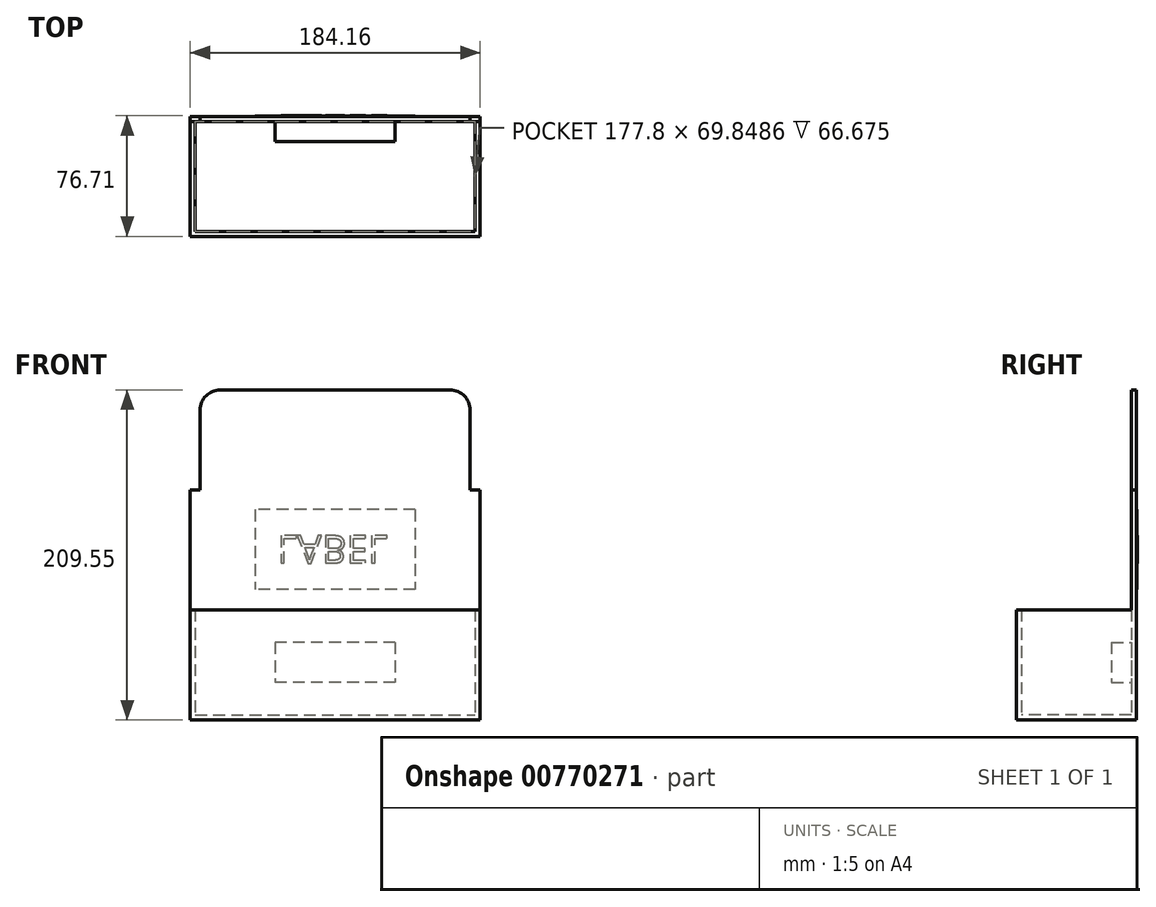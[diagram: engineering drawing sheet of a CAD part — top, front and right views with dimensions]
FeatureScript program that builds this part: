
annotation { "Feature Type Name" : "Feature", "Feature Type Description" : "" }
export const myFeature = defineFeature(function(context is Context, id is Id, definition is map)
    precondition{}
    {
        {
            var Q0;
            Q0=qCreatedBy(makeId("Top.planeOp"),FACE);
            var sketch = newSketch(context, id + "F0", { "sketchPlane" : qUnion([Q0])});
            skLineSegment(sketch, "E0.bottom", {"start": v(92.08, 38.1) * mm, "end": v(-92.08, 38.1) * mm});
            skLineSegment(sketch, "E0.top", {"start": v(92.08, -38.1) * mm, "end": v(-92.08, -38.1) * mm});
            skLineSegment(sketch, "E0.left", {"start": v(92.08, 38.1) * mm, "end": v(92.08, -38.1) * mm});
            skLineSegment(sketch, "E0.right", {"start": v(-92.08, 38.1) * mm, "end": v(-92.08, -38.1) * mm});
            skPoint(sketch, "E0.middle", {"position": v(0, 0) * mm});
            skSolve(sketch);
        }
        {
            var Q0;
            Q0=qSketchRegion(id+"F0",true);
            extrude(context, id + "F1", {"entities" : qUnion([Q0]), "depth" : 3.17 * mm});
        }
        {
            var Q0;
            Q0=makeQuery(id+"F1.opExtrude","CAP_FACE",FACE,{"disambiguationData":[OSD([sQuery(id+"F0.wireOp",EDGE,"E0.bottom"),sQuery(id+"F0.wireOp",EDGE,"E0.top"),sQuery(id+"F0.wireOp",EDGE,"E0.left"),sQuery(id+"F0.wireOp",EDGE,"E0.right")])],"isStart":false});
            var sketch = newSketch(context, id + "F2", { "sketchPlane" : qUnion([Q0])});
            skLineSegment(sketch, "E1.bottom", {"start": v(-92.08, 38.1) * mm, "end": v(-88.9, 38.1) * mm});
            skLineSegment(sketch, "E1.top", {"start": v(-92.08, -38.1) * mm, "end": v(-88.9, -38.1) * mm});
            skLineSegment(sketch, "E1.left", {"start": v(-92.08, 38.1) * mm, "end": v(-92.08, -38.1) * mm});
            skLineSegment(sketch, "E1.right", {"start": v(-88.9, 38.1) * mm, "end": v(-88.9, -38.1) * mm});
            skLineSegment(sketch, "E2.MirrorCS", {"start": v(92.08, 38.1) * mm, "end": v(88.9, 38.1) * mm});
            skLineSegment(sketch, "E3.MirrorCS", {"start": v(88.9, 38.1) * mm, "end": v(88.9, -38.1) * mm});
            skLineSegment(sketch, "E4.MirrorCS", {"start": v(92.08, 38.1) * mm, "end": v(92.08, -38.1) * mm});
            skLineSegment(sketch, "E5.MirrorCS", {"start": v(92.08, -38.1) * mm, "end": v(88.9, -38.1) * mm});
            skLineSegment(sketch, "E6.bottom", {"start": v(-88.9, 38.1) * mm, "end": v(88.9, 38.1) * mm});
            skLineSegment(sketch, "E6.top", {"start": v(-88.9, 34.92) * mm, "end": v(88.9, 34.92) * mm});
            skLineSegment(sketch, "E6.left", {"start": v(-88.9, 38.1) * mm, "end": v(-88.9, 34.92) * mm});
            skLineSegment(sketch, "E6.right", {"start": v(88.9, 38.1) * mm, "end": v(88.9, 34.92) * mm});
            skLineSegment(sketch, "E7.MirrorCS", {"start": v(-88.9, -34.92) * mm, "end": v(88.9, -34.92) * mm});
            skLineSegment(sketch, "E8.MirrorCS", {"start": v(-88.9, -38.1) * mm, "end": v(88.9, -38.1) * mm});
            skSolve(sketch);
        }
        {
            var Q0;
            Q0=qSketchRegion(id+"F2",true);
            extrude(context, id + "F3", {"entities" : qUnion([Q0]), "operationType" : NewBodyOperationType.ADD, "depth" : 66.67 * mm});
        }
        {
            var Q0;
            Q0=makeQuery(id+"F3.opExtrude","CAP_FACE",FACE,{"disambiguationData":[OSD([sQuery(id+"F2.wireOp",EDGE,"E1.bottom"),sQuery(id+"F2.wireOp",EDGE,"E1.top"),sQuery(id+"F2.wireOp",EDGE,"E1.left"),sQuery(id+"F2.wireOp",EDGE,"E1.right"),sQuery(id+"F2.wireOp",EDGE,"E2.MirrorCS"),sQuery(id+"F2.wireOp",EDGE,"E3.MirrorCS"),sQuery(id+"F2.wireOp",EDGE,"E4.MirrorCS"),sQuery(id+"F2.wireOp",EDGE,"E5.MirrorCS"),sQuery(id+"F2.wireOp",EDGE,"E6.bottom"),sQuery(id+"F2.wireOp",EDGE,"E6.top"),sQuery(id+"F2.wireOp",EDGE,"E7.MirrorCS"),sQuery(id+"F2.wireOp",EDGE,"E8.MirrorCS")])],"isStart":false});
            var sketch = newSketch(context, id + "F4", { "sketchPlane" : qUnion([Q0])});
            skLineSegment(sketch, "E9.bottom", {"start": v(-92.08, 38.1) * mm, "end": v(92.08, 38.1) * mm});
            skLineSegment(sketch, "E9.top", {"start": v(-92.08, 34.92) * mm, "end": v(92.08, 34.92) * mm});
            skLineSegment(sketch, "E9.left", {"start": v(-92.08, 38.1) * mm, "end": v(-92.08, 34.92) * mm});
            skLineSegment(sketch, "E9.right", {"start": v(92.08, 38.1) * mm, "end": v(92.08, 34.92) * mm});
            skSolve(sketch);
        }
        {
            var Q0;
            Q0=qSketchRegion(id+"F4",true);
            extrude(context, id + "F5", {"entities" : qUnion([Q0]), "operationType" : NewBodyOperationType.ADD, "depth" : 76.2 * mm});
        }
        {
            var Q0;
            Q0=makeQuery(id+"F5.opExtrude","CAP_FACE",FACE,{"disambiguationData":[OSD([sQuery(id+"F4.wireOp",EDGE,"E9.bottom"),sQuery(id+"F4.wireOp",EDGE,"E9.top"),sQuery(id+"F4.wireOp",EDGE,"E9.left"),sQuery(id+"F4.wireOp",EDGE,"E9.right")])],"isStart":false});
            var sketch = newSketch(context, id + "F6", { "sketchPlane" : qUnion([Q0])});
            skLineSegment(sketch, "E10.bottom", {"start": v(-85.72, 38.1) * mm, "end": v(85.72, 38.1) * mm});
            skLineSegment(sketch, "E10.top", {"start": v(-85.72, 34.92) * mm, "end": v(85.72, 34.92) * mm});
            skLineSegment(sketch, "E10.left", {"start": v(-85.72, 38.1) * mm, "end": v(-85.72, 34.92) * mm});
            skLineSegment(sketch, "E10.right", {"start": v(85.72, 38.1) * mm, "end": v(85.72, 34.92) * mm});
            skSolve(sketch);
        }
        {
            var Q0;
            Q0=qSketchRegion(id+"F6",true);
            extrude(context, id + "F7", {"entities" : qUnion([Q0]), "operationType" : NewBodyOperationType.ADD, "depth" : 63.5 * mm});
        }
        {
            var Q0;
            Q0=makeQuery(id+"F7.opExtrude","CAP_EDGE",EDGE,{"disambiguationData":[OSD([sQuery(id+"F6.wireOp",EDGE,"E10.left")])],"isStart":false});
            var Q1;
            Q1=makeQuery(id+"F7.opExtrude","CAP_EDGE",EDGE,{"disambiguationData":[OSD([sQuery(id+"F6.wireOp",EDGE,"E10.right")])],"isStart":false});
            fillet(context, id + "F8", {"entities" : qUnion([Q0, Q1]), "radius" : 12.7 * mm, "tangentPropagation" : true, "allowEdgeOverflow" : false});
        }
        {
            var Q0;
            Q0=makeQuery(id+"F7.boolean.opBoolean","MERGE",FACE,{"derivedFrom":[makeQuery(id+"F5.boolean.opBoolean","MERGE",FACE,{"derivedFrom":[makeQuery(id+"F3.opExtrude","SWEPT_FACE",FACE,{"disambiguationData":[OSD([sQuery(id+"F2.wireOp",EDGE,"E6.top")])]}),makeQuery(id+"F5.opExtrude","SWEPT_FACE",FACE,{"disambiguationData":[OSD([sQuery(id+"F4.wireOp",EDGE,"E9.top")])]})]}),makeQuery(id+"F7.opExtrude","SWEPT_FACE",FACE,{"disambiguationData":[OSD([sQuery(id+"F6.wireOp",EDGE,"E10.top")])]})]});
            var sketch = newSketch(context, id + "F9", { "sketchPlane" : qUnion([Q0])});
            skLineSegment(sketch, "E11.bottom", {"start": v(38.1, 49.21) * mm, "end": v(-38.1, 49.21) * mm});
            skLineSegment(sketch, "E11.top", {"start": v(38.1, 23.81) * mm, "end": v(-38.1, 23.81) * mm});
            skLineSegment(sketch, "E11.left", {"start": v(38.1, 49.21) * mm, "end": v(38.1, 23.81) * mm});
            skLineSegment(sketch, "E11.right", {"start": v(-38.1, 49.21) * mm, "end": v(-38.1, 23.81) * mm});
            skPoint(sketch, "E11.middle", {"position": v(0, 36.51) * mm});
            skSolve(sketch);
        }
        {
            var Q0;
            Q0=makeQuery(id+"F9.imprint","IMPRINT",FACE,{"disambiguationData":[TD([[makeQuery(id+"F9.imprint","IMPRINT",EDGE,{"derivedFrom":sQuery(id+"F9.wireOp",EDGE,"E11.bottom")}),1.0]])]});
            extrude(context, id + "F10", {"entities" : qUnion([Q0]), "operationType" : NewBodyOperationType.ADD, "depth" : 12.7 * mm});
        }
        {
            var Q0;
            Q0=makeQuery(id+"F7.boolean.opBoolean","MERGE",FACE,{"derivedFrom":[makeQuery(id+"F5.boolean.opBoolean","MERGE",FACE,{"derivedFrom":[makeQuery(id+"F3.boolean.opBoolean","MERGE",FACE,{"derivedFrom":[makeQuery(id+"F1.opExtrude","SWEPT_FACE",FACE,{"disambiguationData":[OSD([sQuery(id+"F0.wireOp",EDGE,"E0.bottom")])]}),makeQuery(id+"F3.opExtrude","SWEPT_FACE",FACE,{"disambiguationData":[OSD([sQuery(id+"F2.wireOp",EDGE,"E1.bottom"),sQuery(id+"F2.wireOp",EDGE,"E2.MirrorCS"),sQuery(id+"F2.wireOp",EDGE,"E6.bottom")])]})]}),makeQuery(id+"F5.opExtrude","SWEPT_FACE",FACE,{"disambiguationData":[OSD([sQuery(id+"F4.wireOp",EDGE,"E9.bottom")])]})]}),makeQuery(id+"F7.opExtrude","SWEPT_FACE",FACE,{"disambiguationData":[OSD([sQuery(id+"F6.wireOp",EDGE,"E10.bottom")])]})]});
            var sketch = newSketch(context, id + "F11", { "sketchPlane" : qUnion([Q0])});
            skLineSegment(sketch, "E12", {"start": v(-85.72, 146.05) * mm, "end": v(85.72, 146.05) * mm});
            skLineSegment(sketch, "E13", {"start": v(92.07, 70.1) * mm, "end": v(-92.07, 70.1) * mm});
            skLineSegment(sketch, "E14", {"start": v(0, 70.1) * mm, "end": v(0, 146.05) * mm});
            skLineSegment(sketch, "E15.bottom", {"start": v(-50.8, 133.47) * mm, "end": v(50.8, 133.47) * mm});
            skLineSegment(sketch, "E15.top", {"start": v(-50.8, 82.67) * mm, "end": v(50.8, 82.67) * mm});
            skLineSegment(sketch, "E15.left", {"start": v(-50.8, 133.47) * mm, "end": v(-50.8, 82.67) * mm});
            skLineSegment(sketch, "E15.right", {"start": v(50.8, 133.47) * mm, "end": v(50.8, 82.67) * mm});
            skPoint(sketch, "E15.middle", {"position": v(0, 108.07) * mm});
            skSolve(sketch);
        }
        {
            var Q0;
            Q0=qSketchRegion(id+"F11",true);
            extrude(context, id + "F12", {"entities" : qUnion([Q0]), "operationType" : NewBodyOperationType.ADD, "depth" : 0.25 * mm});
        }
        {
            var Q0;
            Q0=makeQuery(id+"F12.opExtrude","CAP_FACE",FACE,{"disambiguationData":[OSD([sQuery(id+"F11.wireOp",EDGE,"E15.bottom"),sQuery(id+"F11.wireOp",EDGE,"E15.top"),sQuery(id+"F11.wireOp",EDGE,"E15.left"),sQuery(id+"F11.wireOp",EDGE,"E15.right")])],"isStart":false});
            var sketch = newSketch(context, id + "F13", { "sketchPlane" : qUnion([Q0])});
            skText(sketch, "E16", { "text": "LABEL", "fontName": "OpenSans-Regular.ttf"});
            const initialGuessF13  = {"E16": [0.03675, 0.11698, -1, 0, 0.01757]};
            skSetInitialGuess(sketch, initialGuessF13);
            skSolve(sketch);
        }
        {
            var Q0;
            Q0=qSketchRegion(id+"F13",true);
            extrude(context, id + "F14", {"entities" : qUnion([Q0]), "operationType" : NewBodyOperationType.ADD, "depth" : 0.25 * mm});
        }
    });
